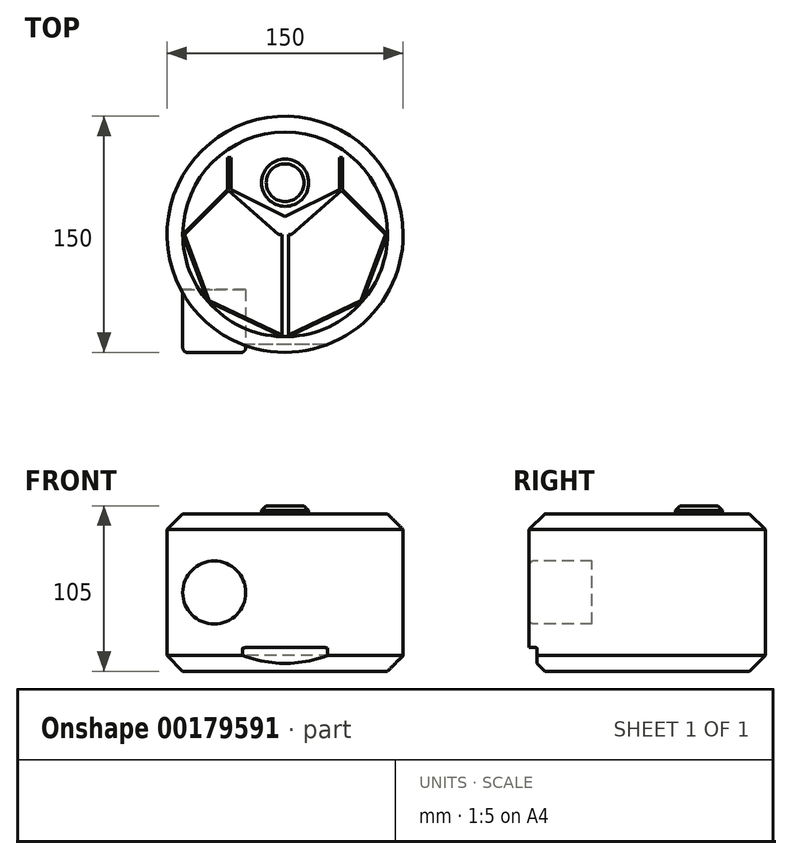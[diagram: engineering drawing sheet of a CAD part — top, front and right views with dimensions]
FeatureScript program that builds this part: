
annotation { "Feature Type Name" : "Feature", "Feature Type Description" : "" }
export const myFeature = defineFeature(function(context is Context, id is Id, definition is map)
    precondition{}
    {
        {
            var Q0;
            Q0=qCreatedBy(makeId("Top.planeOp"),FACE);
            var sketch = newSketch(context, id + "F0", { "sketchPlane" : qUnion([Q0])});
            skCircle(sketch, "E0", {"center": v(0, 0) * mm, "radius": 75 * mm});
            skSolve(sketch);
        }
        {
            var Q0;
            Q0=makeQuery(id+"F0.imprint","IMPRINT",FACE,{"disambiguationData":[TD([[makeQuery(id+"F0.imprint","IMPRINT",EDGE,{"derivedFrom":sQuery(id+"F0.wireOp",EDGE,"E0")}),1.0]])]});
            extrude(context, id + "F1", {"entities" : qUnion([Q0]), "depth" : 100 * mm, "symmetric" : true});
        }
        {
            var Q0;
            Q0=makeQuery(id+"F1.opExtrude","CAP_EDGE",EDGE,{"disambiguationData":[OSD([sQuery(id+"F0.wireOp",EDGE,"E0")])],"isStart":false});
            var Q1;
            Q1=makeQuery(id+"F1.opExtrude","CAP_EDGE",EDGE,{"disambiguationData":[OSD([sQuery(id+"F0.wireOp",EDGE,"E0")])],"isStart":true});
            chamfer(context, id + "F2", {"entities" : qUnion([Q0, Q1]), "width" : 10 * mm, "tangentPropagation" : true});
        }
        {
            var Q0;
            Q0=qCreatedBy(makeId("Front.planeOp"),FACE);
            cPlane(context, id + "F3", {"entities" : qUnion([Q0]), "cplaneType" : CPlaneType.OFFSET, "offset" : 75 * mm, "width" : 150 * mm, "height" : 150 * mm});
        }
        {
            var Q0;
            Q0=qCreatedBy(id+"F3.planeOp",FACE);
            var sketch = newSketch(context, id + "F4", { "sketchPlane" : qUnion([Q0])});
            skCircle(sketch, "E1", {"center": v(-45, 0) * mm, "radius": 20 * mm});
            skCircle(sketch, "E2.MirrorC", {"center": v(45, 0) * mm, "radius": 20 * mm});
            skLineSegment(sketch, "E3.0", {"start": v(-75, -40) * mm, "end": v(75, -40) * mm});
            skLineSegment(sketch, "E4.bottom", {"start": v(25, -35) * mm, "end": v(-25, -35) * mm});
            skLineSegment(sketch, "E4.top", {"start": v(30, -45) * mm, "end": v(-30, -45) * mm});
            skLineSegment(sketch, "E4.left", {"start": v(30, -40) * mm, "end": v(30, -45) * mm});
            skLineSegment(sketch, "E4.right", {"start": v(-30, -40) * mm, "end": v(-30, -45) * mm});
            skPoint(sketch, "E4.middle", {"position": v(0, -40) * mm});
            skPoint(sketch, "E5.visualSharp", {"position": v(-30, -35) * mm});
            skArc(sketch, "E5.filletArc", {"start": v(-25, -35) * mm, "mid": v(-28.54, -36.46) * mm, "end": v(-30, -40) * mm});
            skPoint(sketch, "E6.visualSharp", {"position": v(30, -35) * mm});
            skArc(sketch, "E6.filletArc", {"start": v(30, -40) * mm, "mid": v(28.54, -36.46) * mm, "end": v(25, -35) * mm});
            skSolve(sketch);
        }
        {
            var Q0;
            Q0=makeQuery(id+"F4.imprint","IMPRINT",FACE,{"disambiguationData":[TD([[makeQuery(id+"F4.imprint","IMPRINT",EDGE,{"derivedFrom":sQuery(id+"F4.wireOp",EDGE,"E1")}),1.0]])]});
            var Q1;
            Q1=makeQuery(id+"F4.imprint","IMPRINT",FACE,{"disambiguationData":[TD([[makeQuery(id+"F4.imprint","IMPRINT",EDGE,{"derivedFrom":sQuery(id+"F4.wireOp",EDGE,"E2.MirrorC")}),-1.0]])]});
            extrude(context, id + "F5", {"entities" : qUnion([Q0, Q1]), "oppositeDirection" : true, "depth" : 40 * mm});
        }
        {
            var Q0;
            Q0=makeQuery(id+"F5.opExtrude","CAP_EDGE",EDGE,{"disambiguationData":[OSD([sQuery(id+"F4.wireOp",EDGE,"E1")])],"isStart":true});
            var Q1;
            Q1=makeQuery(id+"F5.opExtrude","CAP_EDGE",EDGE,{"disambiguationData":[OSD([sQuery(id+"F4.wireOp",EDGE,"E2.MirrorC")])],"isStart":true});
            fillet(context, id + "F6", {"entities" : qUnion([Q0, Q1]), "radius" : 3 * mm, "tangentPropagation" : true, "allowEdgeOverflow" : false});
        }
        {
            var Q0;
            Q0=makeQuery(id+"F4.imprint","IMPRINT",FACE,{"disambiguationData":[TD([[makeQuery(id+"F4.imprint","IMPRINT",EDGE,{"derivedFrom":sQuery(id+"F4.wireOp",EDGE,"E4.bottom")}),1.0]])]});
            var Q1;
            Q1=makeQuery(id+"F4.imprint","IMPRINT",FACE,{"disambiguationData":[TD([[makeQuery(id+"F4.imprint","IMPRINT",EDGE,{"derivedFrom":sQuery(id+"F4.wireOp",EDGE,"E4.top")}),-1.0]])]});
            extrude(context, id + "F7", {"entities" : qUnion([Q0, Q1]), "operationType" : NewBodyOperationType.REMOVE, "oppositeDirection" : true, "depth" : 5 * mm});
        }
        {
            var Q0;
            Q0=makeQuery(id+"F1.opExtrude","CAP_FACE",FACE,{"disambiguationData":[OSD([sQuery(id+"F0.wireOp",EDGE,"E0")])],"isStart":false});
            var sketch = newSketch(context, id + "F8", { "sketchPlane" : qUnion([Q0])});
            skCircle(sketch, "E7", {"center": v(0, 32.8) * mm, "radius": 15 * mm});
            skLineSegment(sketch, "E8", {"start": v(0, 0) * mm, "end": v(0, 11.43) * mm});
            skLineSegment(sketch, "E9", {"start": v(0, 11.43) * mm, "end": v(-34.44, 28.57) * mm});
            skLineSegment(sketch, "E10", {"start": v(-34.44, 28.57) * mm, "end": v(-34.44, 48.75) * mm});
            skLineSegment(sketch, "E11", {"start": v(-34.44, 48.75) * mm, "end": v(-36.59, 48.75) * mm});
            skLineSegment(sketch, "E12", {"start": v(-36.59, 48.75) * mm, "end": v(-36.59, 28.57) * mm});
            skLineSegment(sketch, "E13", {"start": v(-36.59, 28.57) * mm, "end": v(-4.09, 0) * mm});
            skLineSegment(sketch, "E14", {"start": v(-4.09, 0) * mm, "end": v(0, 0) * mm});
            skLineSegment(sketch, "E15.MirrorCS", {"start": v(0, 11.43) * mm, "end": v(34.44, 28.57) * mm});
            skLineSegment(sketch, "E16.MirrorCS", {"start": v(36.59, 28.57) * mm, "end": v(4.09, 0) * mm});
            skLineSegment(sketch, "E17.MirrorCS", {"start": v(4.09, 0) * mm, "end": v(0, 0) * mm});
            skLineSegment(sketch, "E18.MirrorCS", {"start": v(34.44, 28.57) * mm, "end": v(34.44, 48.75) * mm});
            skLineSegment(sketch, "E19.MirrorCS", {"start": v(34.44, 48.75) * mm, "end": v(36.59, 48.75) * mm});
            skLineSegment(sketch, "E20.MirrorCS", {"start": v(36.59, 48.75) * mm, "end": v(36.59, 28.57) * mm});
            skLineSegment(sketch, "E21", {"start": v(-2.04, 0) * mm, "end": v(-2.04, -64.97) * mm});
            skLineSegment(sketch, "E22", {"start": v(-2.04, -64.97) * mm, "end": v(-48.97, -42.75) * mm});
            skLineSegment(sketch, "E23", {"start": v(-48.97, -42.75) * mm, "end": v(-65, 0) * mm});
            skLineSegment(sketch, "E24", {"start": v(-65, 0) * mm, "end": v(-36.59, 28.57) * mm});
            skLineSegment(sketch, "E25.0", {"start": v(-63.84, -0.25) * mm, "end": v(-35.84, 27.9) * mm});
            skCircle(sketch, "E26.0", {"center": v(0, 0) * mm, "radius": 70 * mm});
            skLineSegment(sketch, "E27.0", {"start": v(-48.17, -42.02) * mm, "end": v(-63.84, -0.25) * mm});
            skLineSegment(sketch, "E28.0", {"start": v(-2.04, -63.86) * mm, "end": v(-48.17, -42.02) * mm});
            skLineSegment(sketch, "E29", {"start": v(0, 0) * mm, "end": v(0, -65) * mm, "construction": true});
            skLineSegment(sketch, "E30.MirrorCS", {"start": v(2.04, 0) * mm, "end": v(2.04, -64.97) * mm});
            skLineSegment(sketch, "E31.MirrorCS", {"start": v(2.04, -63.86) * mm, "end": v(48.17, -42.02) * mm});
            skLineSegment(sketch, "E32.MirrorCS", {"start": v(2.04, -64.97) * mm, "end": v(48.97, -42.75) * mm});
            skLineSegment(sketch, "E33.MirrorCS", {"start": v(48.17, -42.02) * mm, "end": v(63.84, -0.25) * mm});
            skLineSegment(sketch, "E34.MirrorCS", {"start": v(48.97, -42.75) * mm, "end": v(65, 0) * mm});
            skLineSegment(sketch, "E35.MirrorCS", {"start": v(63.84, -0.25) * mm, "end": v(35.84, 27.9) * mm});
            skLineSegment(sketch, "E36.MirrorCS", {"start": v(65, 0) * mm, "end": v(36.59, 28.57) * mm});
            skPoint(sketch, "E37.orphan", {"position": v(-35.88, 27.87) * mm});
            skPoint(sketch, "E38.orphan", {"position": v(35.88, 27.87) * mm});
            skSolve(sketch);
        }
        {
            var Q0;
            Q0=makeQuery(id+"F8.imprint","IMPRINT",FACE,{"disambiguationData":[TD([[makeQuery(id+"F8.imprint","IMPRINT",EDGE,{"derivedFrom":sQuery(id+"F8.wireOp",EDGE,"E7")}),1.0]])]});
            extrude(context, id + "F9", {"entities" : qUnion([Q0]), "operationType" : NewBodyOperationType.ADD, "depth" : 5 * mm});
        }
        {
            var Q0;
            Q0=makeQuery(id+"F8.imprint","IMPRINT",FACE,{"disambiguationData":[TD([[makeQuery(id+"F8.imprint","IMPRINT",EDGE,{"derivedFrom":sQuery(id+"F8.wireOp",EDGE,"E8")}),-1.0]])]});
            var Q1;
            Q1=makeQuery(id+"F8.imprint","IMPRINT",FACE,{"disambiguationData":[TD([[makeQuery(id+"F8.imprint","IMPRINT",EDGE,{"derivedFrom":sQuery(id+"F8.wireOp",EDGE,"E8")}),1.0]])]});
            var Q2;
            {var subQ0=sQuery(id+"F8.wireOp",EDGE,"E22");Q2=makeQuery(id+"F8.imprint","IMPRINT",FACE,{"disambiguationData":[TD([[makeQuery(id+"F8.imprint","IMPRINT",EDGE,{"derivedFrom":subQ0}),-1.0]])]});}
            var Q3;
            {var subQ1=sQuery(id+"F8.wireOp",EDGE,"E31.MirrorCS");Q3=makeQuery(id+"F8.imprint","IMPRINT",FACE,{"disambiguationData":[TD([[makeQuery(id+"F8.imprint","IMPRINT",EDGE,{"derivedFrom":subQ1}),-1.0]])]});}
            var Q4;
            {var subQ0=sQuery(id+"F8.wireOp",EDGE,"E21");var subQ1=sQuery(id+"F8.wireOp",EDGE,"E14");var subQ2=makeQuery(id+"F8.imprint","INTERSECT",VERTEX,{"derivedFrom":[subQ1,subQ0]});Q4=makeQuery(id+"F8.imprint","IMPRINT",FACE,{"disambiguationData":[TD([[makeQuery(id+"F8.imprint","IMPRINT",EDGE,{"disambiguationData":[TD([[subQ2,-1.0]])],"derivedFrom":subQ0}),1.0]])]});}
            extrude(context, id + "F10", {"entities" : qUnion([Q0, Q1, Q2, Q3, Q4]), "operationType" : NewBodyOperationType.REMOVE, "oppositeDirection" : true, "depth" : .5 * mm});
        }
        {
            var Q0;
            Q0=makeQuery(id+"F9.opExtrude","CAP_EDGE",EDGE,{"disambiguationData":[OSD([sQuery(id+"F8.wireOp",EDGE,"E7")])],"isStart":false});
            chamfer(context, id + "F11", {"entities" : qUnion([Q0]), "width" : 3 * mm, "tangentPropagation" : true});
        }
    });
